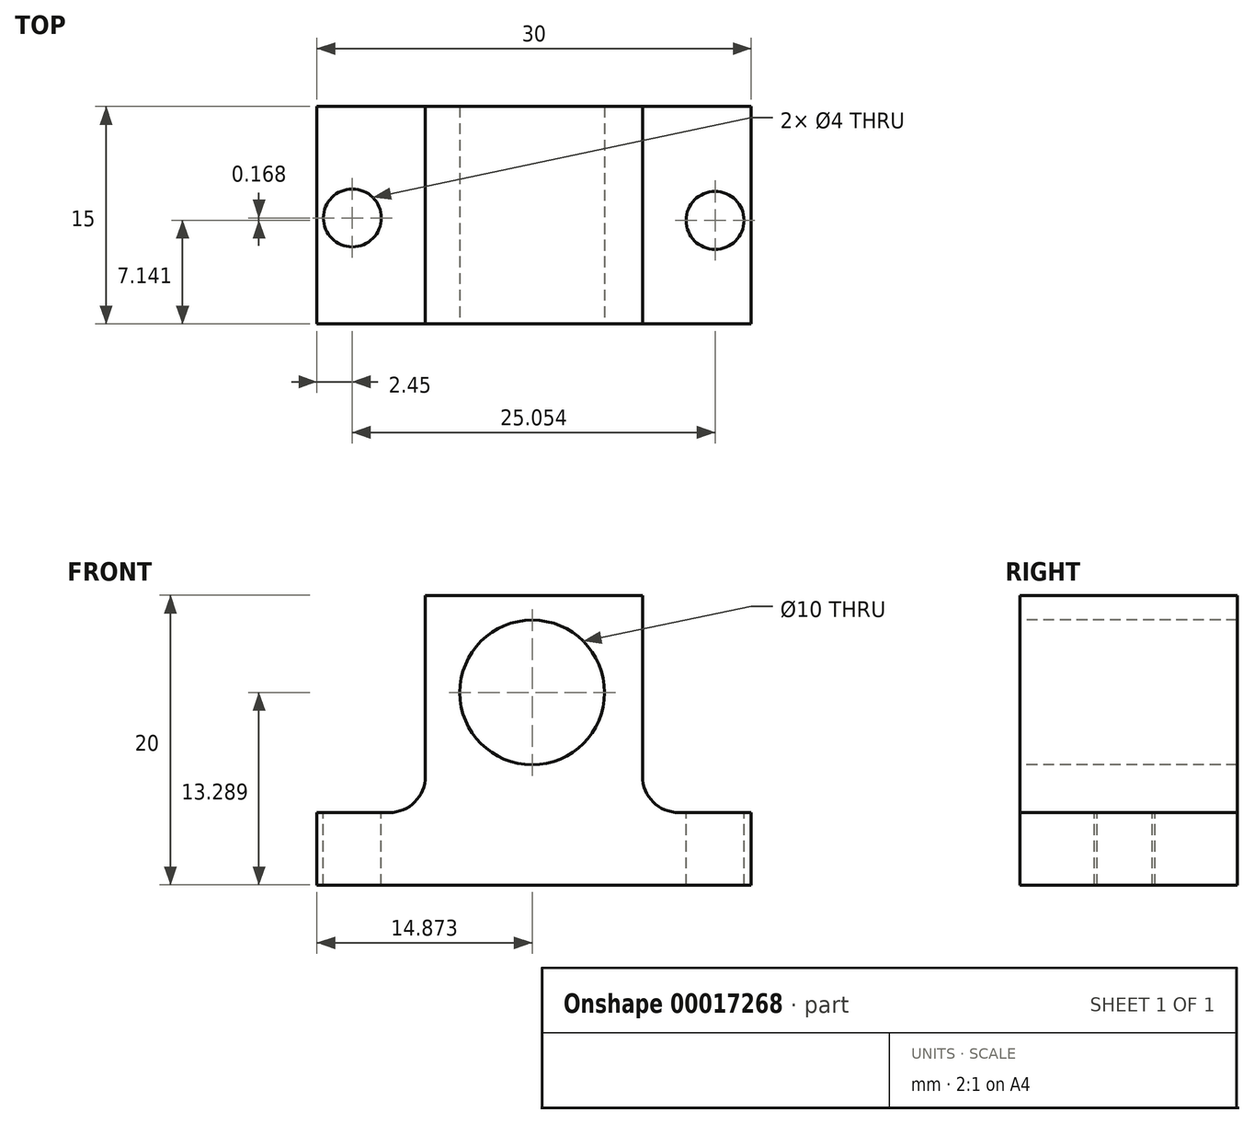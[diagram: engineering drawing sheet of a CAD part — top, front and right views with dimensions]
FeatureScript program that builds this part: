
annotation { "Feature Type Name" : "Feature", "Feature Type Description" : "" }
export const myFeature = defineFeature(function(context is Context, id is Id, definition is map)
    precondition{}
    {
        {
            var Q0;
            Q0=qCreatedBy(makeId("Front.planeOp"),FACE);
            var sketch = newSketch(context, id + "F0", { "sketchPlane" : qUnion([Q0])});
            skLineSegment(sketch, "E0", {"start": v(-9.26, 14.48) * mm, "end": v(-9.26, 9.48) * mm});
            skLineSegment(sketch, "E1", {"start": v(-9.26, 9.48) * mm, "end": v(20.74, 9.48) * mm});
            skLineSegment(sketch, "E2", {"start": v(20.74, 9.48) * mm, "end": v(20.74, 14.48) * mm});
            skLineSegment(sketch, "E3", {"start": v(20.74, 14.48) * mm, "end": v(15.74, 14.48) * mm});
            skLineSegment(sketch, "E4", {"start": v(-9.26, 14.48) * mm, "end": v(-4.26, 14.48) * mm});
            skLineSegment(sketch, "E5", {"start": v(-1.76, 16.98) * mm, "end": v(-1.76, 29.48) * mm});
            skLineSegment(sketch, "E6", {"start": v(-1.76, 29.48) * mm, "end": v(13.24, 29.48) * mm});
            skLineSegment(sketch, "E7", {"start": v(13.24, 29.48) * mm, "end": v(13.24, 16.98) * mm});
            skPoint(sketch, "E8.visualSharp", {"position": v(-1.76, 14.48) * mm});
            skArc(sketch, "E8.filletArc", {"start": v(-4.26, 14.48) * mm, "mid": v(-2.5, 15.2) * mm, "end": v(-1.76, 16.98) * mm});
            skPoint(sketch, "E9.visualSharp", {"position": v(13.24, 14.48) * mm});
            skArc(sketch, "E9.filletArc", {"start": v(13.24, 16.98) * mm, "mid": v(13.97, 15.2) * mm, "end": v(15.74, 14.48) * mm});
            skSolve(sketch);
        }
        {
            var Q0;
            Q0=makeQuery(id+"F0.imprint","IMPRINT",FACE,{"disambiguationData":[TD([[makeQuery(id+"F0.imprint","IMPRINT",EDGE,{"derivedFrom":sQuery(id+"F0.wireOp",EDGE,"E0")}),1.0]])]});
            extrude(context, id + "F1", {"entities" : qUnion([Q0]), "depth" : 15 * mm});
        }
        {
            var Q0;
            Q0=makeQuery(id+"F1.opExtrude","CAP_FACE",FACE,{"disambiguationData":[OSD([sQuery(id+"F0.wireOp",EDGE,"E0"),sQuery(id+"F0.wireOp",EDGE,"E1"),sQuery(id+"F0.wireOp",EDGE,"E2"),sQuery(id+"F0.wireOp",EDGE,"E3"),sQuery(id+"F0.wireOp",EDGE,"E4"),sQuery(id+"F0.wireOp",EDGE,"E5"),sQuery(id+"F0.wireOp",EDGE,"E6"),sQuery(id+"F0.wireOp",EDGE,"E7"),sQuery(id+"F0.wireOp",EDGE,"E8.filletArc"),sQuery(id+"F0.wireOp",EDGE,"E9.filletArc")])],"isStart":false});
            var sketch = newSketch(context, id + "F2", { "sketchPlane" : qUnion([Q0])});
            skCircle(sketch, "E10", {"center": v(5.61, 22.77) * mm, "radius": 5 * mm});
            skSolve(sketch);
        }
        {
            var Q0;
            Q0 = qSketchRegion(id + "F2", true);
            extrude(context, id + "F3", {"entities" : qUnion([Q0]), "operationType" : NewBodyOperationType.REMOVE, "endBound" : BoundingType.THROUGH_ALL, "oppositeDirection" : true, "depth" : 25 * mm});
        }
        {
            var Q0;
            Q0=makeQuery(id+"F1.opExtrude","SWEPT_FACE",FACE,{"disambiguationData":[OSD([sQuery(id+"F0.wireOp",EDGE,"E3")])]});
            var sketch = newSketch(context, id + "F4", { "sketchPlane" : qUnion([Q0])});
            skCircle(sketch, "E11", {"center": v(18.24, -7.86) * mm, "radius": 2 * mm});
            skSolve(sketch);
        }
        {
            var Q0;
            Q0 = qSketchRegion(id + "F4", true);
            extrude(context, id + "F5", {"entities" : qUnion([Q0]), "operationType" : NewBodyOperationType.REMOVE, "endBound" : BoundingType.THROUGH_ALL, "oppositeDirection" : true, "depth" : 25 * mm});
        }
        {
            var Q0;
            Q0=makeQuery(id+"F1.opExtrude","SWEPT_FACE",FACE,{"disambiguationData":[OSD([sQuery(id+"F0.wireOp",EDGE,"E4")])]});
            var sketch = newSketch(context, id + "F6", { "sketchPlane" : qUnion([Q0])});
            skCircle(sketch, "E12", {"center": v(-6.81, -7.7) * mm, "radius": 2 * mm});
            skSolve(sketch);
        }
        {
            var Q0;
            Q0 = qSketchRegion(id + "F6", true);
            extrude(context, id + "F7", {"entities" : qUnion([Q0]), "operationType" : NewBodyOperationType.REMOVE, "endBound" : BoundingType.THROUGH_ALL, "oppositeDirection" : true, "depth" : 25 * mm});
        }
    });
